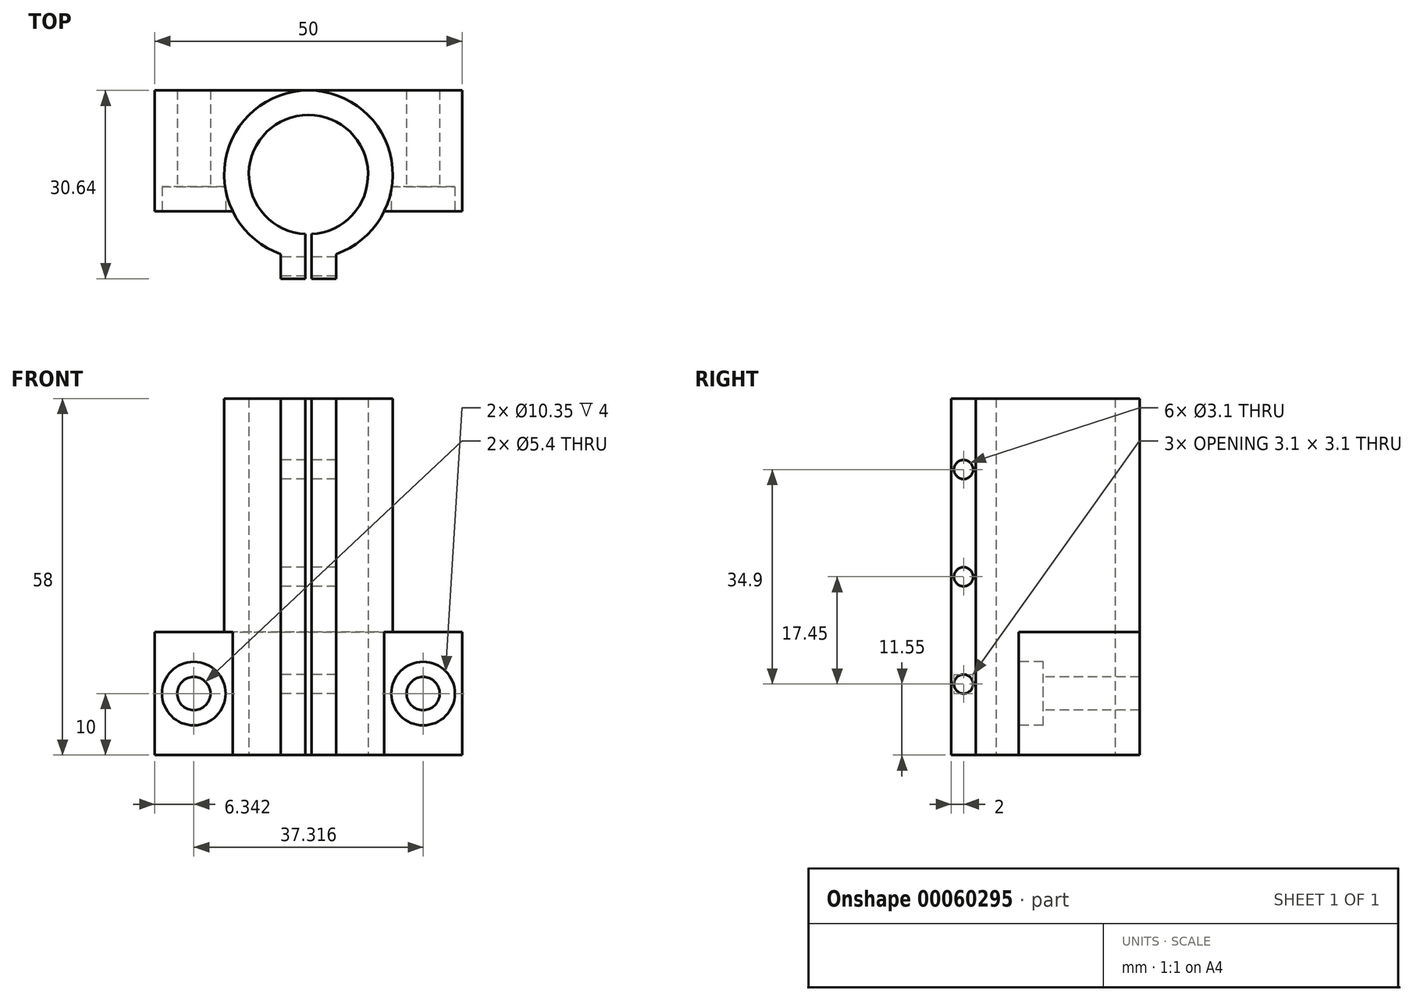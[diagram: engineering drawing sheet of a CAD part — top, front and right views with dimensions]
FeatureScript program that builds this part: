
annotation { "Feature Type Name" : "Feature", "Feature Type Description" : "" }
export const myFeature = defineFeature(function(context is Context, id is Id, definition is map)
    precondition{}
    {
        {
            var Q0;
            Q0=qCreatedBy(makeId("Top.planeOp"),FACE);
            var sketch = newSketch(context, id + "F0", { "sketchPlane" : qUnion([Q0])});
            skLineSegment(sketch, "E0.bottom", {"start": v(-25, 13.7) * mm, "end": v(25, 13.7) * mm});
            skLineSegment(sketch, "E0.top", {"start": v(-25, -14) * mm, "end": v(25, -14) * mm});
            skLineSegment(sketch, "E0.left", {"start": v(-25, 13.7) * mm, "end": v(-25, -14) * mm});
            skLineSegment(sketch, "E0.right", {"start": v(25, 13.7) * mm, "end": v(25, -14) * mm});
            skCircle(sketch, "E1", {"center": v(0, 0) * mm, "radius": 9.7 * mm});
            skLineSegment(sketch, "E2", {"start": v(0, 0) * mm, "end": v(0.5, 0) * mm});
            skLineSegment(sketch, "E3", {"start": v(0.5, 0) * mm, "end": v(0.5, -13.7) * mm});
            skCircle(sketch, "E4", {"center": v(0, 0) * mm, "radius": 13.7 * mm});
            skLineSegment(sketch, "E5", {"start": v(0.5, -13.7) * mm, "end": v(0.5, -16.94) * mm});
            skLineSegment(sketch, "E6", {"start": v(0.5, -16.94) * mm, "end": v(4.5, -16.94) * mm});
            skLineSegment(sketch, "E7", {"start": v(4.5, -16.94) * mm, "end": v(4.5, -12.94) * mm});
            skLineSegment(sketch, "E8.MirrorCS", {"start": v(-0.5, -13.7) * mm, "end": v(-0.5, -16.94) * mm});
            skLineSegment(sketch, "E9.MirrorCS", {"start": v(-0.5, -16.94) * mm, "end": v(-4.5, -16.94) * mm});
            skLineSegment(sketch, "E10.MirrorCS", {"start": v(-4.5, -16.94) * mm, "end": v(-4.5, -12.94) * mm});
            skLineSegment(sketch, "E11.MirrorCS", {"start": v(-0.5, 0) * mm, "end": v(-0.5, -13.7) * mm});
            skLineSegment(sketch, "E12.MirrorCS", {"start": v(0, 0) * mm, "end": v(-0.5, 0) * mm});
            skLineSegment(sketch, "E13", {"start": v(-25, -6) * mm, "end": v(25, -6) * mm});
            skSolve(sketch);
        }
        {
            var Q0;
            {var subQ1=sQuery(id+"F0.wireOp",EDGE,"E0.bottom");var subQ7=sQuery(id+"F0.wireOp",EDGE,"E0.left");var subQ8=makeQuery(id+"F0.imprint","INTERSECT",VERTEX,{"derivedFrom":[subQ1,subQ7]});Q0=makeQuery(id+"F0.imprint","IMPRINT",FACE,{"disambiguationData":[TD([[makeQuery(id+"F0.imprint","IMPRINT",EDGE,{"disambiguationData":[TD([[subQ8,-1.0]])],"derivedFrom":subQ1}),-1.0]])]});}
            var Q1;
            {var subQ1=sQuery(id+"F0.wireOp",EDGE,"E0.bottom");var subQ7=sQuery(id+"F0.wireOp",EDGE,"E0.right");var subQ8=makeQuery(id+"F0.imprint","INTERSECT",VERTEX,{"derivedFrom":[subQ1,subQ7]});Q1=makeQuery(id+"F0.imprint","IMPRINT",FACE,{"disambiguationData":[TD([[makeQuery(id+"F0.imprint","IMPRINT",EDGE,{"disambiguationData":[TD([[subQ8,1.0]])],"derivedFrom":subQ1}),-1.0]])]});}
            extrude(context, id + "F1", {"entities" : qUnion([Q0, Q1]), "depth" : 20 * mm});
        }
        {
            var Q0;
            {var subQ0=sQuery(id+"F0.wireOp",EDGE,"E13");var subQ1=sQuery(id+"F0.wireOp",EDGE,"E1");var subQ2=makeQuery(id+"F0.imprint","INTERSECT",VERTEX,{"disambiguationData":[OD(0.0)],"derivedFrom":[subQ1,subQ0]});Q0=makeQuery(id+"F0.imprint","IMPRINT",FACE,{"disambiguationData":[TD([[makeQuery(id+"F0.imprint","IMPRINT",EDGE,{"disambiguationData":[TD([[subQ2,1.0]])],"derivedFrom":subQ1}),-1.0]])]});}
            var Q1;
            {var subQ0=sQuery(id+"F0.wireOp",EDGE,"OeIoF8mI-yU0Q-JgbS-M2l9-rrvGmHEVIJVL");var subQ1=sQuery(id+"F0.wireOp",EDGE,"E1");var subQ2=makeQuery(id+"F0.imprint","INTERSECT",VERTEX,{"disambiguationData":[OD(0.0)],"derivedFrom":[subQ1,subQ0]});Q1=makeQuery(id+"F0.imprint","IMPRINT",FACE,{"disambiguationData":[TD([[makeQuery(id+"F0.imprint","IMPRINT",EDGE,{"disambiguationData":[TD([[subQ2,1.0]])],"derivedFrom":subQ1}),-1.0]])]});}
            var Q2;
            {var subQ4=sQuery(id+"F0.wireOp",EDGE,"E13");var subQ5=sQuery(id+"F0.wireOp",EDGE,"E1");var subQ6=makeQuery(id+"F0.imprint","INTERSECT",VERTEX,{"disambiguationData":[OD(0.0)],"derivedFrom":[subQ5,subQ4]});Q2=makeQuery(id+"F0.imprint","IMPRINT",FACE,{"disambiguationData":[TD([[makeQuery(id+"F0.imprint","IMPRINT",EDGE,{"disambiguationData":[TD([[subQ6,-1.0]])],"derivedFrom":subQ5}),-1.0]])]});}
            var Q3;
            {var subQ4=sQuery(id+"F0.wireOp",EDGE,"E3");var subQ6=sQuery(id+"F0.wireOp",EDGE,"E1");var subQ7=makeQuery(id+"F0.imprint","INTERSECT",VERTEX,{"derivedFrom":[subQ6,subQ4]});Q3=makeQuery(id+"F0.imprint","IMPRINT",FACE,{"disambiguationData":[TD([[makeQuery(id+"F0.imprint","IMPRINT",EDGE,{"disambiguationData":[TD([[subQ7,-1.0]])],"derivedFrom":subQ6}),-1.0]])]});}
            var Q4;
            {var subQ5=sQuery(id+"F0.wireOp",EDGE,"E6");Q4=makeQuery(id+"F0.imprint","IMPRINT",FACE,{"disambiguationData":[TD([[makeQuery(id+"F0.imprint","IMPRINT",EDGE,{"derivedFrom":subQ5}),1.0]])]});}
            var Q5;
            {var subQ0=sQuery(id+"F0.wireOp",EDGE,"E5");var subQ1=sQuery(id+"F0.wireOp",EDGE,"E0.top");var subQ2=makeQuery(id+"F0.imprint","INTERSECT",VERTEX,{"derivedFrom":[subQ1,subQ0]});Q5=makeQuery(id+"F0.imprint","IMPRINT",FACE,{"disambiguationData":[TD([[makeQuery(id+"F0.imprint","IMPRINT",EDGE,{"disambiguationData":[TD([[subQ2,-1.0]])],"derivedFrom":subQ1}),1.0]])]});}
            var Q6;
            {var subQ0=sQuery(id+"F0.wireOp",EDGE,"E10.MirrorCS");var subQ1=sQuery(id+"F0.wireOp",EDGE,"E0.top");var subQ2=makeQuery(id+"F0.imprint","INTERSECT",VERTEX,{"derivedFrom":[subQ1,subQ0]});Q6=makeQuery(id+"F0.imprint","IMPRINT",FACE,{"disambiguationData":[TD([[makeQuery(id+"F0.imprint","IMPRINT",EDGE,{"disambiguationData":[TD([[subQ2,-1.0]])],"derivedFrom":subQ1}),1.0]])]});}
            var Q7;
            {var subQ5=sQuery(id+"F0.wireOp",EDGE,"E9.MirrorCS");Q7=makeQuery(id+"F0.imprint","IMPRINT",FACE,{"disambiguationData":[TD([[makeQuery(id+"F0.imprint","IMPRINT",EDGE,{"derivedFrom":subQ5}),-1.0]])]});}
            extrude(context, id + "F2", {"entities" : qUnion([Q0, Q1, Q2, Q3, Q4, Q5, Q6, Q7]), "operationType" : NewBodyOperationType.ADD, "depth" : 58 * mm});
        }
        {
            var Q0;
            {var subQ0=sQuery(id+"F0.wireOp",EDGE,"E13");Q0=makeQuery(id+"F1.opExtrude","SWEPT_FACE",FACE,{"disambiguationData":[OSD([subQ0]),TDD([makeQuery(id+"F0.imprint","IMPRINT",EDGE,{"disambiguationData":[TD([[makeQuery(id+"F0.imprint","INTERSECT",VERTEX,{"derivedFrom":[sQuery(id+"F0.wireOp",EDGE,"E0.left"),subQ0]}),-1.0]])],"derivedFrom":subQ0})])]});}
            var sketch = newSketch(context, id + "F3", { "sketchPlane" : qUnion([Q0])});
            skLineSegment(sketch, "E14", {"start": v(-25, 10) * mm, "end": v(25, 10) * mm});
            skCircle(sketch, "E15", {"center": v(-18.66, 10) * mm, "radius": 5.17 * mm});
            skCircle(sketch, "E16", {"center": v(-18.66, 10) * mm, "radius": 2.7 * mm});
            skCircle(sketch, "E17.MirrorC", {"center": v(18.66, 10) * mm, "radius": 5.17 * mm});
            skCircle(sketch, "E18.MirrorC", {"center": v(18.66, 10) * mm, "radius": 2.7 * mm});
            skSolve(sketch);
        }
        {
            var Q0;
            {var subQ0=sQuery(id+"F3.wireOp",EDGE,"E15");var subQ1=sQuery(id+"F3.wireOp",EDGE,"E14");var subQ2=makeQuery(id+"F3.imprint","INTERSECT",VERTEX,{"disambiguationData":[OD(0.0)],"derivedFrom":[subQ1,subQ0]});Q0=makeQuery(id+"F3.imprint","IMPRINT",FACE,{"disambiguationData":[TD([[makeQuery(id+"F3.imprint","IMPRINT",EDGE,{"disambiguationData":[TD([[subQ2,-1.0]])],"derivedFrom":subQ1}),1.0]])]});}
            var Q1;
            {var subQ0=sQuery(id+"F3.wireOp",EDGE,"E15");var subQ1=sQuery(id+"F3.wireOp",EDGE,"E14");var subQ2=makeQuery(id+"F3.imprint","INTERSECT",VERTEX,{"disambiguationData":[OD(0.0)],"derivedFrom":[subQ1,subQ0]});Q1=makeQuery(id+"F3.imprint","IMPRINT",FACE,{"disambiguationData":[TD([[makeQuery(id+"F3.imprint","IMPRINT",EDGE,{"disambiguationData":[TD([[subQ2,-1.0]])],"derivedFrom":subQ1}),-1.0]])]});}
            var Q2;
            {var subQ0=sQuery(id+"F3.wireOp",EDGE,"E17.MirrorC");var subQ1=sQuery(id+"F3.wireOp",EDGE,"E14");var subQ2=makeQuery(id+"F3.imprint","INTERSECT",VERTEX,{"disambiguationData":[OD(0.0)],"derivedFrom":[subQ1,subQ0]});Q2=makeQuery(id+"F3.imprint","IMPRINT",FACE,{"disambiguationData":[TD([[makeQuery(id+"F3.imprint","IMPRINT",EDGE,{"disambiguationData":[TD([[subQ2,-1.0]])],"derivedFrom":subQ1}),1.0]])]});}
            var Q3;
            {var subQ0=sQuery(id+"F3.wireOp",EDGE,"E17.MirrorC");var subQ1=sQuery(id+"F3.wireOp",EDGE,"E14");var subQ2=makeQuery(id+"F3.imprint","INTERSECT",VERTEX,{"disambiguationData":[OD(0.0)],"derivedFrom":[subQ1,subQ0]});Q3=makeQuery(id+"F3.imprint","IMPRINT",FACE,{"disambiguationData":[TD([[makeQuery(id+"F3.imprint","IMPRINT",EDGE,{"disambiguationData":[TD([[subQ2,-1.0]])],"derivedFrom":subQ1}),-1.0]])]});}
            extrude(context, id + "F4", {"entities" : qUnion([Q0, Q1, Q2, Q3]), "operationType" : NewBodyOperationType.REMOVE, "oppositeDirection" : true, "depth" : 4 * mm});
        }
        {
            var Q0;
            {var subQ0=sQuery(id+"F0.wireOp",EDGE,"E13");Q0=makeQuery(id+"F4.boolean.opBoolean","SPLIT",FACE,{"disambiguationData":[TD([makeQuery(id+"F4.opExtrude","SWEPT_FACE",FACE,{"disambiguationData":[OSD([sQuery(id+"F3.wireOp",EDGE,"E16")])]})])],"derivedFrom":makeQuery(id+"F1.opExtrude","SWEPT_FACE",FACE,{"disambiguationData":[OSD([subQ0]),TDD([makeQuery(id+"F0.imprint","IMPRINT",EDGE,{"disambiguationData":[TD([[makeQuery(id+"F0.imprint","INTERSECT",VERTEX,{"derivedFrom":[sQuery(id+"F0.wireOp",EDGE,"E0.left"),subQ0]}),-1.0]])],"derivedFrom":subQ0})])]})});}
            var Q1;
            {var subQ0=sQuery(id+"F0.wireOp",EDGE,"E13");Q1=makeQuery(id+"F4.boolean.opBoolean","SPLIT",FACE,{"disambiguationData":[TD([makeQuery(id+"F4.opExtrude","SWEPT_FACE",FACE,{"disambiguationData":[OSD([sQuery(id+"F3.wireOp",EDGE,"E18.MirrorC")])]})])],"derivedFrom":makeQuery(id+"F1.opExtrude","SWEPT_FACE",FACE,{"disambiguationData":[OSD([subQ0]),TDD([makeQuery(id+"F0.imprint","IMPRINT",EDGE,{"disambiguationData":[TD([[makeQuery(id+"F0.imprint","INTERSECT",VERTEX,{"derivedFrom":[sQuery(id+"F0.wireOp",EDGE,"E0.right"),subQ0]}),1.0]])],"derivedFrom":subQ0})])]})});}
            extrude(context, id + "F5", {"entities" : qUnion([Q0, Q1]), "operationType" : NewBodyOperationType.REMOVE, "oppositeDirection" : true, "depth" : 20 * mm});
        }
        {
            var Q0;
            Q0=makeQuery(id+"F2.opExtrude","SWEPT_FACE",FACE,{"disambiguationData":[OSD([sQuery(id+"F0.wireOp",EDGE,"E10.MirrorCS")])]});
            var sketch = newSketch(context, id + "F6", { "sketchPlane" : qUnion([Q0])});
            skLineSegment(sketch, "E19", {"start": v(14.94, 58) * mm, "end": v(14.94, 0) * mm});
            skCircle(sketch, "E20", {"center": v(14.94, 46.45) * mm, "radius": 1.55 * mm});
            skLineSegment(sketch, "E21", {"start": v(14.94, 29) * mm, "end": v(16.94, 29) * mm});
            skCircle(sketch, "E22.MirrorC", {"center": v(14.94, 11.55) * mm, "radius": 1.55 * mm});
            skCircle(sketch, "E23", {"center": v(14.94, 29) * mm, "radius": 1.55 * mm});
            skSolve(sketch);
        }
        {
            var Q0;
            Q0 = qSketchRegion(id + "F6", true);
            extrude(context, id + "F7", {"entities" : qUnion([Q0]), "operationType" : NewBodyOperationType.REMOVE, "oppositeDirection" : true, "depth" : 9 * mm});
        }
    });
